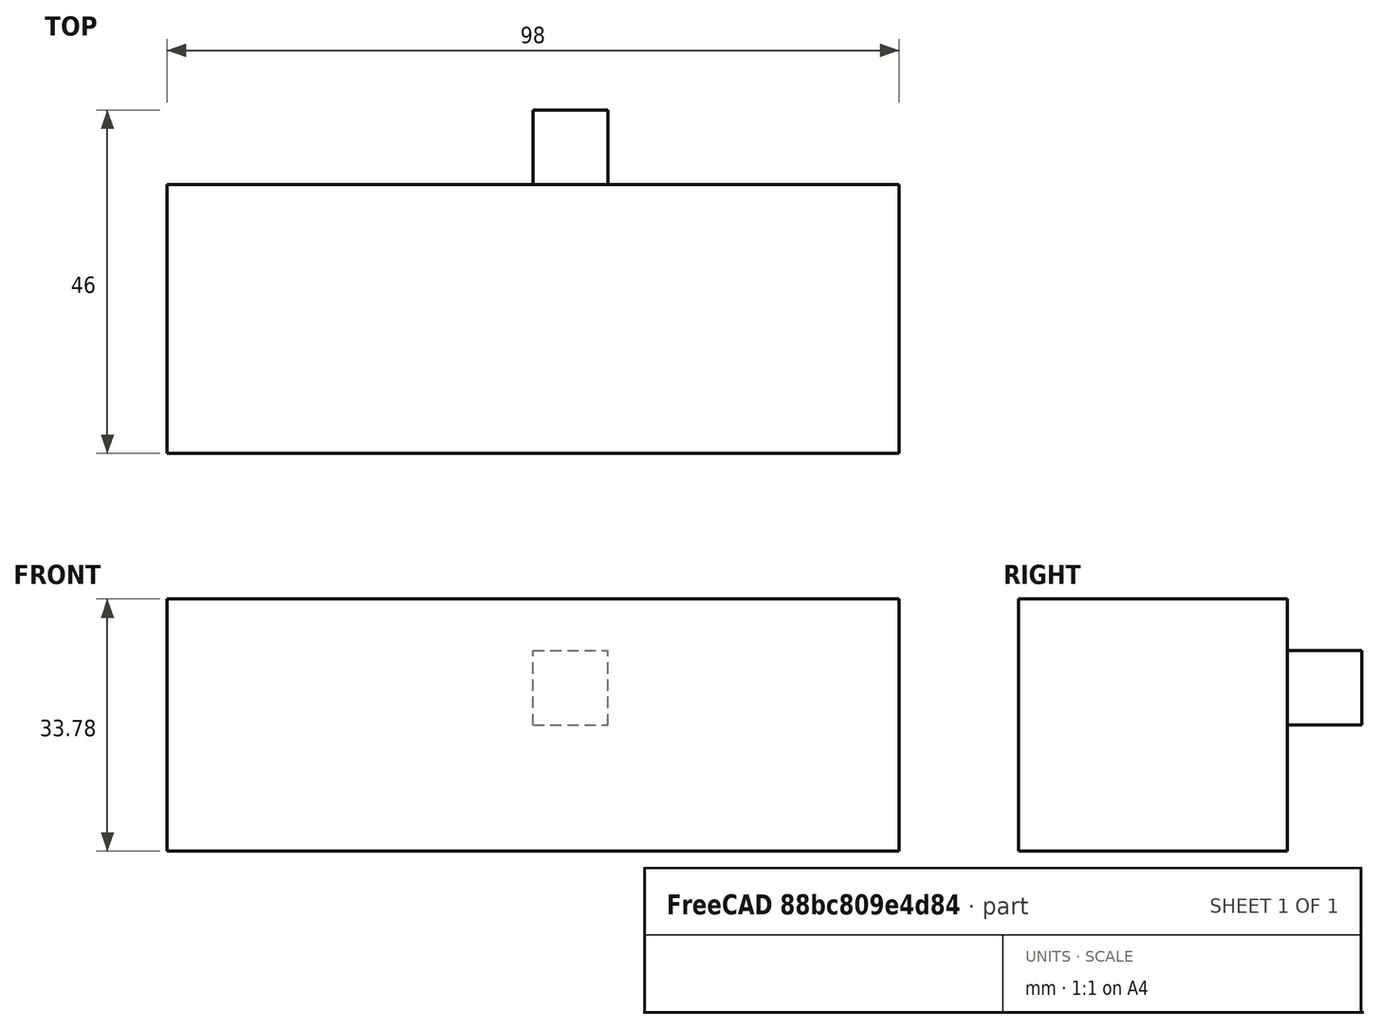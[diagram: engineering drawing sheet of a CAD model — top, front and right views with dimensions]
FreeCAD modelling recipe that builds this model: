
FCSTD DOCUMENT  (FreeCAD 0.21R33771 (Git))
Label: textures
License: All rights reserved
LicenseURL: http://en.wikipedia.org/wiki/All_rights_reserved
objects: Sketcher::SketchObject×1, Part::Box×1, App::MaterialObjectPython×1, PartDesign::Pad×1, PartDesign::Body×1, App::DocumentObjectGroupPython×1, App::FeaturePython×1
note: 5 computed .brp shape members not serialized (recipe doc carries the construction recipe); baked Part::Feature solids carry a one-line shape summary decoded from their .brp

FEATURE [Sketcher::SketchObject] Sketch
  FullyConstrained = false
  MapMode = 5
  Placement = pos=(0,0,0) rot=(1,0,0;1.5708rad)
  Support = -> [XZ_Plane]
  sketch-geometry (5):
    g0: LineSegment StartX=-49.0017 StartY=16.8885 StartZ=0 EndX=-49.0017 EndY=-16.8885 EndZ=0
    g1: LineSegment StartX=-49.0017 StartY=-16.8885 StartZ=0 EndX=49.0017 EndY=-16.8885 EndZ=0
    g2: LineSegment StartX=49.0017 StartY=-16.8885 StartZ=0 EndX=49.0017 EndY=16.8885 EndZ=0
    g3: LineSegment StartX=49.0017 StartY=16.8885 StartZ=0 EndX=-49.0017 EndY=16.8885 EndZ=0
    g4: GeomPoint X=0 Y=0 Z=0
  constraints (10):
    c: Coincident(g0,g1)
    c: Coincident(g1,g2)
    c: Coincident(g2,g3)
    c: Coincident(g3,g0)
    c: Horizontal(g1)
    c: Horizontal(g3)
    c: Vertical(g0)
    c: Vertical(g2)
    c: Symmetric(g1,g0,g4)
    c: Coincident(g4,g-1)
FEATURE [Part::Box] Box  label="Cube"
  AttacherType = Attacher::AttachEngine3D
  Height = 10
  Length = 10
  Width = 10
FEATURE [App::MaterialObjectPython] Material  label="Graphite"  # material (typed FeaturePython)
  Description = Typical material properties for pure graphite
  Material = AuthorAndLicense=Uwe Stöhr, LGPL,CardName=Graphite,Color=(0.8, 0.8, 0.8, 1.0),CompressiveStrength=120.000 MPa,Density=1750.000 kg/m^3,+20 more (map truncated)
  Transparency = 0
FEATURE [PartDesign::Pad] Pad
  Direction = (0,-1,2e-16)
  Length = 36
  Length2 = 10
  Material = -> Material
  Placement = pos=(0,0,0) rot=(1,0,0;1.5708rad)
  Profile = -> Sketch
  ReferenceAxis = -> Sketch [N_Axis]
  Refine = true
  Type = 0
FEATURE [PartDesign::Body] Body
  Group = -> [Sketch,Pad]
  Origin = -> Origin
  Tip = -> Pad
FEATURE [App::DocumentObjectGroupPython] MaterialContainer  label="Materials"  # scripted group (container) (typed FeaturePython)
  Group = -> [Material]
FEATURE [App::FeaturePython] TextureConfig  # WARN: FeaturePython — macro-defined, semantics opaque (R4)
